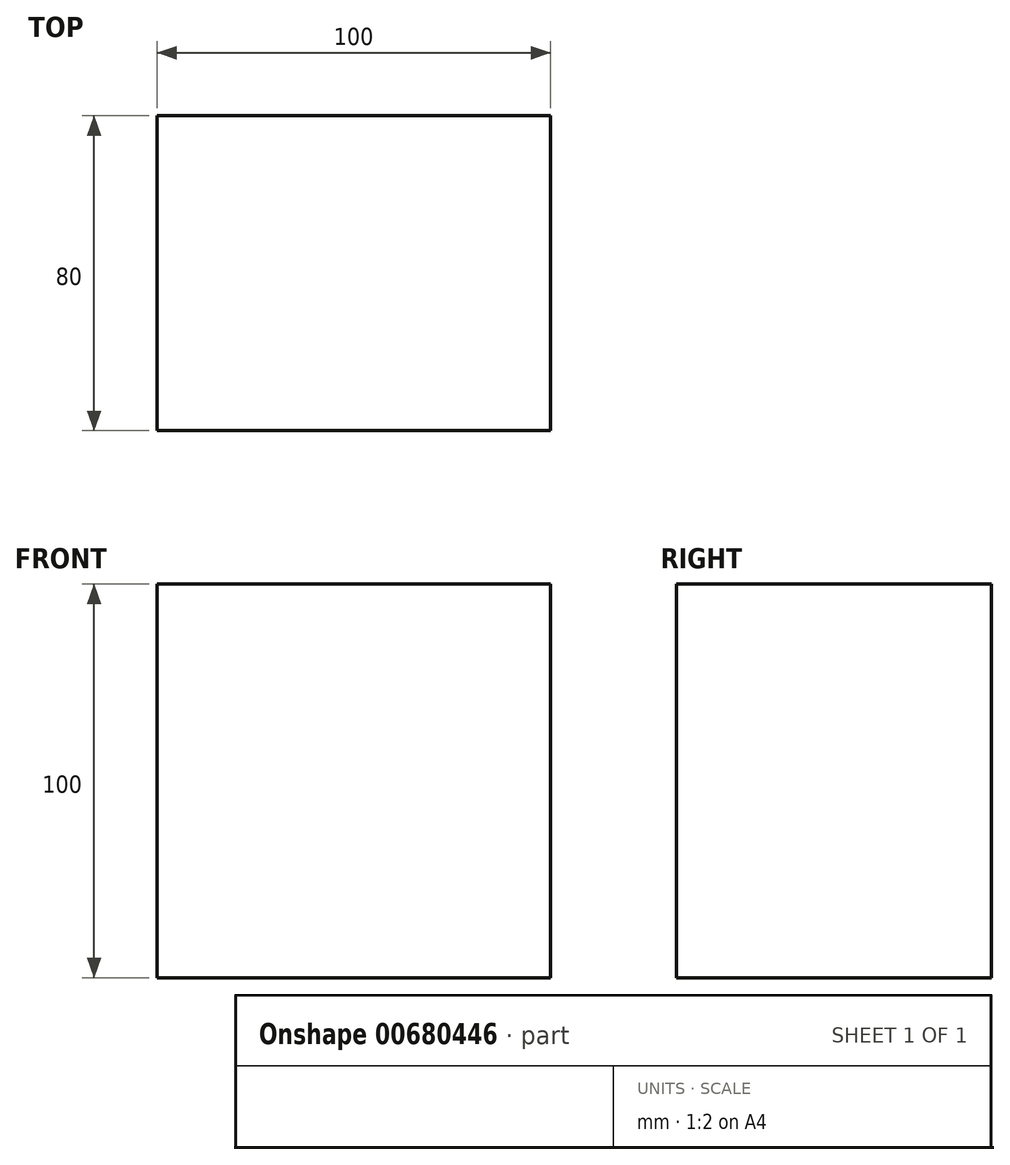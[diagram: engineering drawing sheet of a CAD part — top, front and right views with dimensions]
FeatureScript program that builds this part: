
annotation { "Feature Type Name" : "Feature", "Feature Type Description" : "" }
export const myFeature = defineFeature(function(context is Context, id is Id, definition is map)
    precondition{}
    {
        {
            var Q0;
            Q0=qCreatedBy(makeId("Top.planeOp"),FACE);
            var sketch = newSketch(context, id + "F0", { "sketchPlane" : qUnion([Q0])});
            skLineSegment(sketch, "E0.bottom", {"start": v(-50, 40) * mm, "end": v(50, 40) * mm});
            skLineSegment(sketch, "E0.top", {"start": v(-50, -40) * mm, "end": v(50, -40) * mm});
            skLineSegment(sketch, "E0.left", {"start": v(-50, 40) * mm, "end": v(-50, -40) * mm});
            skLineSegment(sketch, "E0.right", {"start": v(50, 40) * mm, "end": v(50, -40) * mm});
            skPoint(sketch, "E0.middle", {"position": v(0, 0) * mm});
            skSolve(sketch);
        }
        {
            var Q0;
            Q0 = qSketchRegion(id + "F0", true);
            extrude(context, id + "F1", {"entities" : qUnion([Q0]), "depth" : 100 * mm, "offsetDistance" : 25 * mm});
        }
        {
            var Q0;
            Q0=qCreatedBy(makeId("Top.planeOp"),FACE);
            cPlane(context, id + "F2", {"entities" : qUnion([Q0]), "cplaneType" : CPlaneType.OFFSET, "offset" : 100 * mm, "width" : 150 * mm, "height" : 150 * mm});
        }
    });
